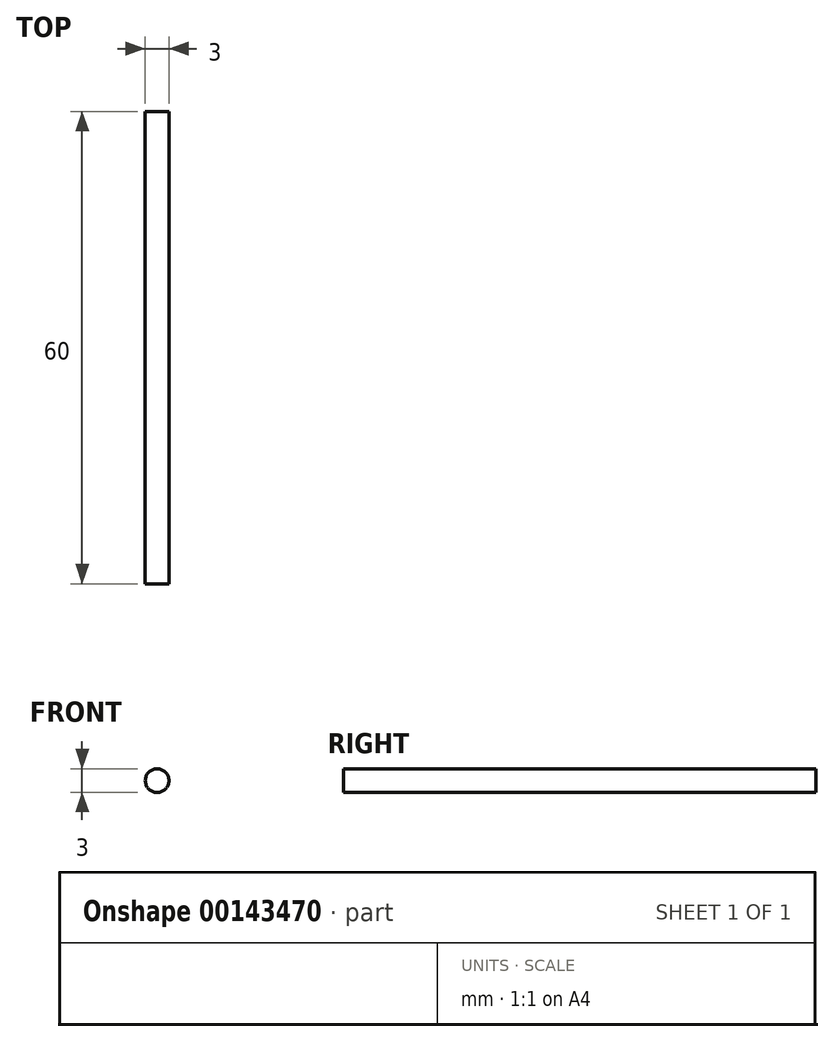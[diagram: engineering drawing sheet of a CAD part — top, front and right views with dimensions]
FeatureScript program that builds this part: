
annotation { "Feature Type Name" : "Feature", "Feature Type Description" : "" }
export const myFeature = defineFeature(function(context is Context, id is Id, definition is map)
    precondition{}
    {
        {
            var Q0;
            Q0=qCreatedBy(makeId("Front.planeOp"),FACE);
            var sketch = newSketch(context, id + "F0", { "sketchPlane" : qUnion([Q0])});
            skCircle(sketch, "E0", {"center": v(0, 0) * mm, "radius": 1.5 * mm});
            skSolve(sketch);
        }
        {
            var Q0;
            Q0=qSketchRegion(id+"F0",true);
            extrude(context, id + "F1", {"entities" : qUnion([Q0]), "endBound" : BoundingType.SYMMETRIC, "depth" : 60 * mm});
        }
    });
